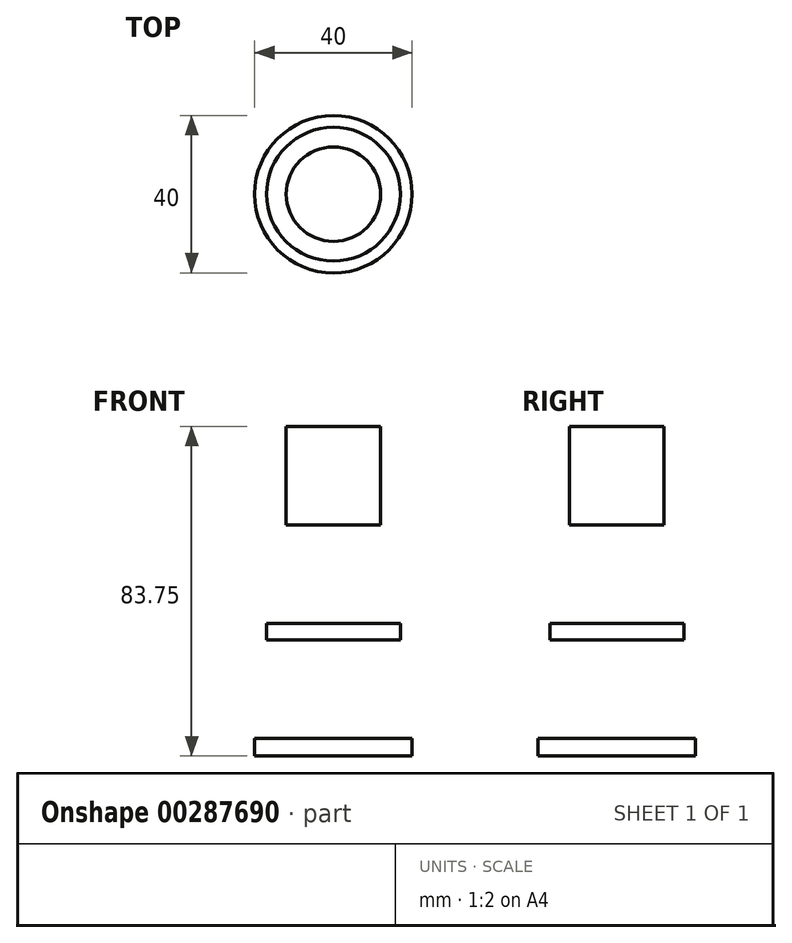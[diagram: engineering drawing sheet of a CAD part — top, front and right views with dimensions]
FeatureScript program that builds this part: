
annotation { "Feature Type Name" : "Feature", "Feature Type Description" : "" }
export const myFeature = defineFeature(function(context is Context, id is Id, definition is map)
    precondition{}
    {
        {
            var Q0;
            Q0=qCreatedBy(makeId("Top.planeOp"),FACE);
            var sketch = newSketch(context, id + "F0", { "sketchPlane" : qUnion([Q0])});
            skCircle(sketch, "E0", {"center": v(0, 0) * mm, "radius": 20 * mm});
            skSolve(sketch);
        }
        {
            var Q0;
            Q0=qSketchRegion(id+"F0",true);
            extrude(context, id + "F1", {"entities" : qUnion([Q0]), "depth" : 4.5 * mm});
        }
        {
            var Q0;
            Q0=makeQuery(id+"F1.opExtrude","CAP_FACE",FACE,{"disambiguationData":[OSD([sQuery(id+"F0.wireOp",EDGE,"E0")])],"isStart":false});
            cPlane(context, id + "F2", {"entities" : qUnion([Q0]), "cplaneType" : CPlaneType.OFFSET, "offset" : 25 * mm, "width" : 150 * mm, "height" : 150 * mm});
        }
        {
            var Q0;
            Q0=qCreatedBy(id+"F2.planeOp",FACE);
            var sketch = newSketch(context, id + "F3", { "sketchPlane" : qUnion([Q0])});
            skCircle(sketch, "E1", {"center": v(0, 0) * mm, "radius": 17 * mm});
            skSolve(sketch);
        }
        {
            var Q0;
            Q0=qSketchRegion(id+"F3",true);
            extrude(context, id + "F4", {"entities" : qUnion([Q0]), "depth" : 4.25 * mm});
        }
        {
            var Q0;
            Q0=makeQuery(id+"F4.opExtrude","CAP_FACE",FACE,{"disambiguationData":[OSD([sQuery(id+"F3.wireOp",EDGE,"E1")])],"isStart":false});
            cPlane(context, id + "F5", {"entities" : qUnion([Q0]), "cplaneType" : CPlaneType.OFFSET, "offset" : 25 * mm, "width" : 150 * mm, "height" : 150 * mm});
        }
        {
            var Q0;
            Q0=qCreatedBy(id+"F5.planeOp",FACE);
            var sketch = newSketch(context, id + "F6", { "sketchPlane" : qUnion([Q0])});
            skCircle(sketch, "E2", {"center": v(0, 0) * mm, "radius": 12 * mm});
            skSolve(sketch);
        }
        {
            var Q0;
            Q0=qSketchRegion(id+"F6",true);
            extrude(context, id + "F7", {"entities" : qUnion([Q0]), "depth" : 25 * mm});
        }
    });
